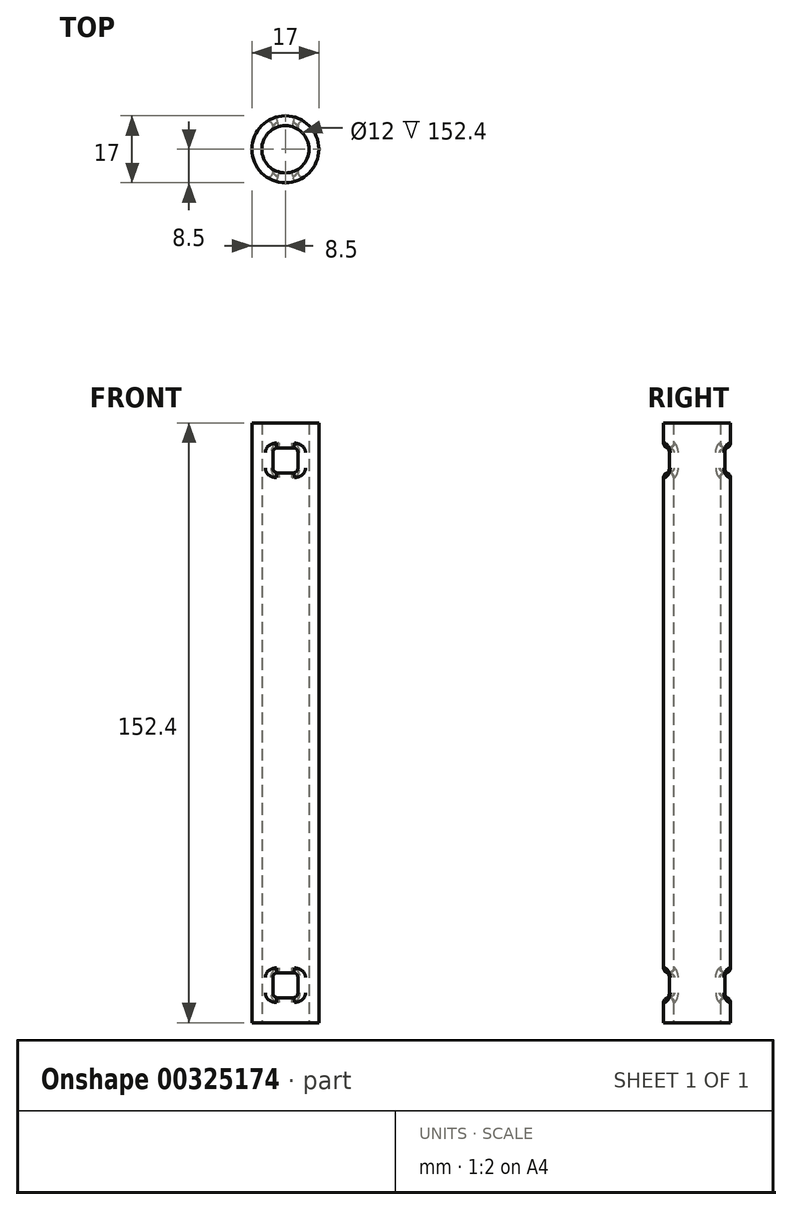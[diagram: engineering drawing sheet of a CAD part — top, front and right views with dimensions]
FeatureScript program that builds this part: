
annotation { "Feature Type Name" : "Feature", "Feature Type Description" : "" }
export const myFeature = defineFeature(function(context is Context, id is Id, definition is map)
    precondition{}
    {
        {
            var Q0;
            Q0=qCreatedBy(makeId("Top.planeOp"),FACE);
            var sketch = newSketch(context, id + "F0", { "sketchPlane" : qUnion([Q0])});
            skCircle(sketch, "E0", {"center": v(0, 0) * mm, "radius": 8.5 * mm});
            skCircle(sketch, "E1", {"center": v(0, 0) * mm, "radius": 6 * mm});
            skSolve(sketch);
        }
        {
            var Q0;
            Q0=makeQuery(id+"F0.imprint","IMPRINT",FACE,{"disambiguationData":[TD([[makeQuery(id+"F0.imprint","IMPRINT",EDGE,{"derivedFrom":sQuery(id+"F0.wireOp",EDGE,"E0")}),1.0]])]});
            extrude(context, id + "F1", {"entities" : qUnion([Q0]), "depth" : 152.4 * mm});
        }
        {
            var Q0;
            Q0=qCreatedBy(makeId("Front.planeOp"),FACE);
            var sketch = newSketch(context, id + "F2", { "sketchPlane" : qUnion([Q0])});
            skLineSegment(sketch, "E2.bottom", {"start": v(3.17, 12.7) * mm, "end": v(-3.18, 12.7) * mm});
            skLineSegment(sketch, "E2.top", {"start": v(3.17, 6.35) * mm, "end": v(-3.18, 6.35) * mm});
            skLineSegment(sketch, "E2.left", {"start": v(3.17, 12.7) * mm, "end": v(3.17, 6.35) * mm});
            skLineSegment(sketch, "E2.right", {"start": v(-3.18, 12.7) * mm, "end": v(-3.18, 6.35) * mm});
            skPoint(sketch, "E2.middle", {"position": v(0, 9.53) * mm});
            skLineSegment(sketch, "E3.bottom", {"start": v(3.17, 146.05) * mm, "end": v(-3.18, 146.05) * mm});
            skLineSegment(sketch, "E3.top", {"start": v(3.17, 139.7) * mm, "end": v(-3.18, 139.7) * mm});
            skLineSegment(sketch, "E3.left", {"start": v(3.17, 146.05) * mm, "end": v(3.17, 139.7) * mm});
            skLineSegment(sketch, "E3.right", {"start": v(-3.18, 146.05) * mm, "end": v(-3.18, 139.7) * mm});
            skPoint(sketch, "E3.middle", {"position": v(0, 142.88) * mm});
            skSolve(sketch);
        }
        {
            var Q0;
            Q0=makeQuery(id+"F2.imprint","IMPRINT",FACE,{"disambiguationData":[TD([[makeQuery(id+"F2.imprint","IMPRINT",EDGE,{"derivedFrom":sQuery(id+"F2.wireOp",EDGE,"E3.bottom")}),1.0]])]});
            var Q1;
            Q1=makeQuery(id+"F2.imprint","IMPRINT",FACE,{"disambiguationData":[TD([[makeQuery(id+"F2.imprint","IMPRINT",EDGE,{"derivedFrom":sQuery(id+"F2.wireOp",EDGE,"E2.bottom")}),1.0]])]});
            extrude(context, id + "F3", {"entities" : qUnion([Q0, Q1]), "operationType" : NewBodyOperationType.REMOVE, "depth" : 25.4 * mm, "hasSecondDirection" : true, "secondDirectionOppositeDirection" : true, "secondDirectionDepth" : 25.4 * mm});
        }
        {
            var Q0;
            Q0=makeQuery(id+"F3.boolean.opBoolean","COPY",FACE,{"disambiguationData":[OD(1.0)],"derivedFrom":makeQuery(id+"F3.opExtrude","SWEPT_FACE",FACE,{"disambiguationData":[OSD([sQuery(id+"F2.wireOp",EDGE,"E3.bottom")])]})});
            var Q1;
            Q1=makeQuery(id+"F3.boolean.opBoolean","INTERSECT",EDGE,{"disambiguationData":[OD(1.0)],"derivedFrom":[makeQuery(id+"F1.opExtrude","SWEPT_FACE",FACE,{"disambiguationData":[OSD([sQuery(id+"F0.wireOp",EDGE,"E1")])]}),makeQuery(id+"F3.opExtrude","SWEPT_FACE",FACE,{"disambiguationData":[OSD([sQuery(id+"F2.wireOp",EDGE,"E3.top")])]})]});
            var Q2;
            Q2=makeQuery(id+"F3.boolean.opBoolean","COPY",FACE,{"disambiguationData":[OD(0.0)],"derivedFrom":makeQuery(id+"F3.opExtrude","SWEPT_FACE",FACE,{"disambiguationData":[OSD([sQuery(id+"F2.wireOp",EDGE,"E3.right")])]})});
            var Q3;
            Q3=makeQuery(id+"F3.boolean.opBoolean","INTERSECT",EDGE,{"disambiguationData":[OD(0.0)],"derivedFrom":[makeQuery(id+"F1.opExtrude","SWEPT_FACE",FACE,{"disambiguationData":[OSD([sQuery(id+"F0.wireOp",EDGE,"E1")])]}),makeQuery(id+"F3.opExtrude","SWEPT_FACE",FACE,{"disambiguationData":[OSD([sQuery(id+"F2.wireOp",EDGE,"E3.right")])]})]});
            var Q4;
            Q4=makeQuery(id+"F3.boolean.opBoolean","INTERSECT",EDGE,{"disambiguationData":[OD(1.0)],"derivedFrom":[makeQuery(id+"F1.opExtrude","SWEPT_FACE",FACE,{"disambiguationData":[OSD([sQuery(id+"F0.wireOp",EDGE,"E0")])]}),makeQuery(id+"F3.opExtrude","SWEPT_FACE",FACE,{"disambiguationData":[OSD([sQuery(id+"F2.wireOp",EDGE,"E3.top")])]})]});
            var Q5;
            Q5=makeQuery(id+"F3.boolean.opBoolean","INTERSECT",EDGE,{"disambiguationData":[OD(1.0)],"derivedFrom":[makeQuery(id+"F1.opExtrude","SWEPT_FACE",FACE,{"disambiguationData":[OSD([sQuery(id+"F0.wireOp",EDGE,"E1")])]}),makeQuery(id+"F3.opExtrude","SWEPT_FACE",FACE,{"disambiguationData":[OSD([sQuery(id+"F2.wireOp",EDGE,"E3.bottom")])]})]});
            var Q6;
            Q6=makeQuery(id+"F3.boolean.opBoolean","COPY",FACE,{"disambiguationData":[OD(0.0)],"derivedFrom":makeQuery(id+"F3.opExtrude","SWEPT_FACE",FACE,{"disambiguationData":[OSD([sQuery(id+"F2.wireOp",EDGE,"E3.left")])]})});
            var Q7;
            Q7=makeQuery(id+"F3.boolean.opBoolean","COPY",FACE,{"disambiguationData":[OD(1.0)],"derivedFrom":makeQuery(id+"F3.opExtrude","SWEPT_FACE",FACE,{"disambiguationData":[OSD([sQuery(id+"F2.wireOp",EDGE,"E3.right")])]})});
            var Q8;
            Q8=makeQuery(id+"F3.boolean.opBoolean","COPY",FACE,{"disambiguationData":[OD(1.0)],"derivedFrom":makeQuery(id+"F3.opExtrude","SWEPT_FACE",FACE,{"disambiguationData":[OSD([sQuery(id+"F2.wireOp",EDGE,"E3.left")])]})});
            var Q9;
            Q9=makeQuery(id+"F3.boolean.opBoolean","COPY",FACE,{"disambiguationData":[OD(1.0)],"derivedFrom":makeQuery(id+"F3.opExtrude","SWEPT_FACE",FACE,{"disambiguationData":[OSD([sQuery(id+"F2.wireOp",EDGE,"E3.top")])]})});
            var Q10;
            Q10=makeQuery(id+"F3.boolean.opBoolean","COPY",FACE,{"disambiguationData":[OD(0.0)],"derivedFrom":makeQuery(id+"F3.opExtrude","SWEPT_FACE",FACE,{"disambiguationData":[OSD([sQuery(id+"F2.wireOp",EDGE,"E3.bottom")])]})});
            var Q11;
            Q11=makeQuery(id+"F3.boolean.opBoolean","COPY",FACE,{"disambiguationData":[OD(0.0)],"derivedFrom":makeQuery(id+"F3.opExtrude","SWEPT_FACE",FACE,{"disambiguationData":[OSD([sQuery(id+"F2.wireOp",EDGE,"E3.top")])]})});
            var Q12;
            Q12=makeQuery(id+"F3.boolean.opBoolean","INTERSECT",EDGE,{"disambiguationData":[OD(1.0)],"derivedFrom":[makeQuery(id+"F1.opExtrude","SWEPT_FACE",FACE,{"disambiguationData":[OSD([sQuery(id+"F0.wireOp",EDGE,"E0")])]}),makeQuery(id+"F3.opExtrude","SWEPT_FACE",FACE,{"disambiguationData":[OSD([sQuery(id+"F2.wireOp",EDGE,"E3.right")])]})]});
            var Q13;
            Q13=makeQuery(id+"F3.boolean.opBoolean","INTERSECT",EDGE,{"disambiguationData":[OD(1.0)],"derivedFrom":[makeQuery(id+"F1.opExtrude","SWEPT_FACE",FACE,{"disambiguationData":[OSD([sQuery(id+"F0.wireOp",EDGE,"E0")])]}),makeQuery(id+"F3.opExtrude","SWEPT_FACE",FACE,{"disambiguationData":[OSD([sQuery(id+"F2.wireOp",EDGE,"E3.bottom")])]})]});
            var Q14;
            Q14=makeQuery(id+"F3.boolean.opBoolean","INTERSECT",EDGE,{"disambiguationData":[OD(0.0)],"derivedFrom":[makeQuery(id+"F1.opExtrude","SWEPT_FACE",FACE,{"disambiguationData":[OSD([sQuery(id+"F0.wireOp",EDGE,"E0")])]}),makeQuery(id+"F3.opExtrude","SWEPT_FACE",FACE,{"disambiguationData":[OSD([sQuery(id+"F2.wireOp",EDGE,"E3.right")])]})]});
            var Q15;
            Q15=makeQuery(id+"F3.boolean.opBoolean","INTERSECT",EDGE,{"disambiguationData":[OD(0.0)],"derivedFrom":[makeQuery(id+"F1.opExtrude","SWEPT_FACE",FACE,{"disambiguationData":[OSD([sQuery(id+"F0.wireOp",EDGE,"E0")])]}),makeQuery(id+"F3.opExtrude","SWEPT_FACE",FACE,{"disambiguationData":[OSD([sQuery(id+"F2.wireOp",EDGE,"E3.bottom")])]})]});
            var Q16;
            Q16=makeQuery(id+"F3.boolean.opBoolean","INTERSECT",EDGE,{"disambiguationData":[OD(0.0)],"derivedFrom":[makeQuery(id+"F1.opExtrude","SWEPT_FACE",FACE,{"disambiguationData":[OSD([sQuery(id+"F0.wireOp",EDGE,"E0")])]}),makeQuery(id+"F3.opExtrude","SWEPT_FACE",FACE,{"disambiguationData":[OSD([sQuery(id+"F2.wireOp",EDGE,"E3.left")])]})]});
            var Q17;
            Q17=makeQuery(id+"F3.boolean.opBoolean","INTERSECT",EDGE,{"disambiguationData":[OD(0.0)],"derivedFrom":[makeQuery(id+"F1.opExtrude","SWEPT_FACE",FACE,{"disambiguationData":[OSD([sQuery(id+"F0.wireOp",EDGE,"E1")])]}),makeQuery(id+"F3.opExtrude","SWEPT_FACE",FACE,{"disambiguationData":[OSD([sQuery(id+"F2.wireOp",EDGE,"E3.top")])]})]});
            var Q18;
            Q18=makeQuery(id+"F3.boolean.opBoolean","INTERSECT",EDGE,{"disambiguationData":[OD(0.0)],"derivedFrom":[makeQuery(id+"F1.opExtrude","SWEPT_FACE",FACE,{"disambiguationData":[OSD([sQuery(id+"F0.wireOp",EDGE,"E1")])]}),makeQuery(id+"F3.opExtrude","SWEPT_FACE",FACE,{"disambiguationData":[OSD([sQuery(id+"F2.wireOp",EDGE,"E3.bottom")])]})]});
            var Q19;
            Q19=makeQuery(id+"F3.boolean.opBoolean","INTERSECT",EDGE,{"disambiguationData":[OD(0.0)],"derivedFrom":[makeQuery(id+"F1.opExtrude","SWEPT_FACE",FACE,{"disambiguationData":[OSD([sQuery(id+"F0.wireOp",EDGE,"E0")])]}),makeQuery(id+"F3.opExtrude","SWEPT_FACE",FACE,{"disambiguationData":[OSD([sQuery(id+"F2.wireOp",EDGE,"E3.top")])]})]});
            var Q20;
            Q20=makeQuery(id+"F3.boolean.opBoolean","INTERSECT",EDGE,{"disambiguationData":[OD(1.0)],"derivedFrom":[makeQuery(id+"F1.opExtrude","SWEPT_FACE",FACE,{"disambiguationData":[OSD([sQuery(id+"F0.wireOp",EDGE,"E1")])]}),makeQuery(id+"F3.opExtrude","SWEPT_FACE",FACE,{"disambiguationData":[OSD([sQuery(id+"F2.wireOp",EDGE,"E3.right")])]})]});
            var Q21;
            Q21=makeQuery(id+"F3.boolean.opBoolean","COPY",EDGE,{"disambiguationData":[OD(0.0)],"derivedFrom":makeQuery(id+"F3.opExtrude","SWEPT_EDGE",EDGE,{"disambiguationData":[OSD([sQuery(id+"F2.wireOp",EDGE,"E3.bottom"),sQuery(id+"F2.wireOp",EDGE,"E3.right")])]})});
            var Q22;
            Q22=makeQuery(id+"F3.boolean.opBoolean","COPY",EDGE,{"disambiguationData":[OD(1.0)],"derivedFrom":makeQuery(id+"F3.opExtrude","SWEPT_EDGE",EDGE,{"disambiguationData":[OSD([sQuery(id+"F2.wireOp",EDGE,"E3.top"),sQuery(id+"F2.wireOp",EDGE,"E3.left")])]})});
            var Q23;
            Q23=makeQuery(id+"F3.boolean.opBoolean","COPY",EDGE,{"disambiguationData":[OD(1.0)],"derivedFrom":makeQuery(id+"F3.opExtrude","SWEPT_EDGE",EDGE,{"disambiguationData":[OSD([sQuery(id+"F2.wireOp",EDGE,"E3.bottom"),sQuery(id+"F2.wireOp",EDGE,"E3.right")])]})});
            var Q24;
            Q24=makeQuery(id+"F3.boolean.opBoolean","INTERSECT",EDGE,{"disambiguationData":[OD(1.0)],"derivedFrom":[makeQuery(id+"F1.opExtrude","SWEPT_FACE",FACE,{"disambiguationData":[OSD([sQuery(id+"F0.wireOp",EDGE,"E0")])]}),makeQuery(id+"F3.opExtrude","SWEPT_FACE",FACE,{"disambiguationData":[OSD([sQuery(id+"F2.wireOp",EDGE,"E3.left")])]})]});
            var Q25;
            Q25=makeQuery(id+"F3.boolean.opBoolean","COPY",EDGE,{"disambiguationData":[OD(0.0)],"derivedFrom":makeQuery(id+"F3.opExtrude","SWEPT_EDGE",EDGE,{"disambiguationData":[OSD([sQuery(id+"F2.wireOp",EDGE,"E3.bottom"),sQuery(id+"F2.wireOp",EDGE,"E3.left")])]})});
            var Q26;
            Q26=makeQuery(id+"F3.boolean.opBoolean","INTERSECT",EDGE,{"disambiguationData":[OD(1.0)],"derivedFrom":[makeQuery(id+"F1.opExtrude","SWEPT_FACE",FACE,{"disambiguationData":[OSD([sQuery(id+"F0.wireOp",EDGE,"E1")])]}),makeQuery(id+"F3.opExtrude","SWEPT_FACE",FACE,{"disambiguationData":[OSD([sQuery(id+"F2.wireOp",EDGE,"E3.left")])]})]});
            var Q27;
            Q27=makeQuery(id+"F3.boolean.opBoolean","COPY",EDGE,{"disambiguationData":[OD(0.0)],"derivedFrom":makeQuery(id+"F3.opExtrude","SWEPT_EDGE",EDGE,{"disambiguationData":[OSD([sQuery(id+"F2.wireOp",EDGE,"E3.top"),sQuery(id+"F2.wireOp",EDGE,"E3.left")])]})});
            var Q28;
            Q28=makeQuery(id+"F3.boolean.opBoolean","COPY",EDGE,{"disambiguationData":[OD(0.0)],"derivedFrom":makeQuery(id+"F3.opExtrude","SWEPT_EDGE",EDGE,{"disambiguationData":[OSD([sQuery(id+"F2.wireOp",EDGE,"E3.top"),sQuery(id+"F2.wireOp",EDGE,"E3.right")])]})});
            var Q29;
            Q29=makeQuery(id+"F3.boolean.opBoolean","INTERSECT",EDGE,{"disambiguationData":[OD(0.0)],"derivedFrom":[makeQuery(id+"F1.opExtrude","SWEPT_FACE",FACE,{"disambiguationData":[OSD([sQuery(id+"F0.wireOp",EDGE,"E1")])]}),makeQuery(id+"F3.opExtrude","SWEPT_FACE",FACE,{"disambiguationData":[OSD([sQuery(id+"F2.wireOp",EDGE,"E3.left")])]})]});
            var Q30;
            Q30=makeQuery(id+"F3.boolean.opBoolean","COPY",EDGE,{"disambiguationData":[OD(1.0)],"derivedFrom":makeQuery(id+"F3.opExtrude","SWEPT_EDGE",EDGE,{"disambiguationData":[OSD([sQuery(id+"F2.wireOp",EDGE,"E3.bottom"),sQuery(id+"F2.wireOp",EDGE,"E3.left")])]})});
            var Q31;
            Q31=makeQuery(id+"F3.boolean.opBoolean","COPY",EDGE,{"disambiguationData":[OD(1.0)],"derivedFrom":makeQuery(id+"F3.opExtrude","SWEPT_EDGE",EDGE,{"disambiguationData":[OSD([sQuery(id+"F2.wireOp",EDGE,"E3.top"),sQuery(id+"F2.wireOp",EDGE,"E3.right")])]})});
            var Q32;
            Q32=makeQuery(id+"F3.boolean.opBoolean","INTERSECT",EDGE,{"disambiguationData":[OD(0.0)],"derivedFrom":[makeQuery(id+"F1.opExtrude","SWEPT_FACE",FACE,{"disambiguationData":[OSD([sQuery(id+"F0.wireOp",EDGE,"E0")])]}),makeQuery(id+"F3.opExtrude","SWEPT_FACE",FACE,{"disambiguationData":[OSD([sQuery(id+"F2.wireOp",EDGE,"E2.bottom")])]})]});
            var Q33;
            Q33=makeQuery(id+"F3.boolean.opBoolean","INTERSECT",EDGE,{"disambiguationData":[OD(0.0)],"derivedFrom":[makeQuery(id+"F1.opExtrude","SWEPT_FACE",FACE,{"disambiguationData":[OSD([sQuery(id+"F0.wireOp",EDGE,"E1")])]}),makeQuery(id+"F3.opExtrude","SWEPT_FACE",FACE,{"disambiguationData":[OSD([sQuery(id+"F2.wireOp",EDGE,"E2.right")])]})]});
            var Q34;
            Q34=makeQuery(id+"F3.boolean.opBoolean","INTERSECT",EDGE,{"disambiguationData":[OD(0.0)],"derivedFrom":[makeQuery(id+"F1.opExtrude","SWEPT_FACE",FACE,{"disambiguationData":[OSD([sQuery(id+"F0.wireOp",EDGE,"E1")])]}),makeQuery(id+"F3.opExtrude","SWEPT_FACE",FACE,{"disambiguationData":[OSD([sQuery(id+"F2.wireOp",EDGE,"E2.bottom")])]})]});
            var Q35;
            Q35=makeQuery(id+"F3.boolean.opBoolean","INTERSECT",EDGE,{"disambiguationData":[OD(0.0)],"derivedFrom":[makeQuery(id+"F1.opExtrude","SWEPT_FACE",FACE,{"disambiguationData":[OSD([sQuery(id+"F0.wireOp",EDGE,"E0")])]}),makeQuery(id+"F3.opExtrude","SWEPT_FACE",FACE,{"disambiguationData":[OSD([sQuery(id+"F2.wireOp",EDGE,"E2.top")])]})]});
            var Q36;
            Q36=makeQuery(id+"F3.boolean.opBoolean","INTERSECT",EDGE,{"disambiguationData":[OD(1.0)],"derivedFrom":[makeQuery(id+"F1.opExtrude","SWEPT_FACE",FACE,{"disambiguationData":[OSD([sQuery(id+"F0.wireOp",EDGE,"E1")])]}),makeQuery(id+"F3.opExtrude","SWEPT_FACE",FACE,{"disambiguationData":[OSD([sQuery(id+"F2.wireOp",EDGE,"E2.bottom")])]})]});
            var Q37;
            Q37=makeQuery(id+"F3.boolean.opBoolean","INTERSECT",EDGE,{"disambiguationData":[OD(1.0)],"derivedFrom":[makeQuery(id+"F1.opExtrude","SWEPT_FACE",FACE,{"disambiguationData":[OSD([sQuery(id+"F0.wireOp",EDGE,"E1")])]}),makeQuery(id+"F3.opExtrude","SWEPT_FACE",FACE,{"disambiguationData":[OSD([sQuery(id+"F2.wireOp",EDGE,"E2.top")])]})]});
            var Q38;
            Q38=makeQuery(id+"F3.boolean.opBoolean","INTERSECT",EDGE,{"disambiguationData":[OD(1.0)],"derivedFrom":[makeQuery(id+"F1.opExtrude","SWEPT_FACE",FACE,{"disambiguationData":[OSD([sQuery(id+"F0.wireOp",EDGE,"E1")])]}),makeQuery(id+"F3.opExtrude","SWEPT_FACE",FACE,{"disambiguationData":[OSD([sQuery(id+"F2.wireOp",EDGE,"E2.right")])]})]});
            var Q39;
            Q39=makeQuery(id+"F3.boolean.opBoolean","INTERSECT",EDGE,{"disambiguationData":[OD(1.0)],"derivedFrom":[makeQuery(id+"F1.opExtrude","SWEPT_FACE",FACE,{"disambiguationData":[OSD([sQuery(id+"F0.wireOp",EDGE,"E0")])]}),makeQuery(id+"F3.opExtrude","SWEPT_FACE",FACE,{"disambiguationData":[OSD([sQuery(id+"F2.wireOp",EDGE,"E2.bottom")])]})]});
            var Q40;
            Q40=makeQuery(id+"F3.boolean.opBoolean","INTERSECT",EDGE,{"disambiguationData":[OD(0.0)],"derivedFrom":[makeQuery(id+"F1.opExtrude","SWEPT_FACE",FACE,{"disambiguationData":[OSD([sQuery(id+"F0.wireOp",EDGE,"E0")])]}),makeQuery(id+"F3.opExtrude","SWEPT_FACE",FACE,{"disambiguationData":[OSD([sQuery(id+"F2.wireOp",EDGE,"E2.right")])]})]});
            var Q41;
            Q41=makeQuery(id+"F3.boolean.opBoolean","COPY",EDGE,{"disambiguationData":[OD(1.0)],"derivedFrom":makeQuery(id+"F3.opExtrude","SWEPT_EDGE",EDGE,{"disambiguationData":[OSD([sQuery(id+"F2.wireOp",EDGE,"E2.bottom"),sQuery(id+"F2.wireOp",EDGE,"E2.left")])]})});
            var Q42;
            Q42=makeQuery(id+"F3.boolean.opBoolean","COPY",EDGE,{"disambiguationData":[OD(0.0)],"derivedFrom":makeQuery(id+"F3.opExtrude","SWEPT_EDGE",EDGE,{"disambiguationData":[OSD([sQuery(id+"F2.wireOp",EDGE,"E2.bottom"),sQuery(id+"F2.wireOp",EDGE,"E2.right")])]})});
            var Q43;
            Q43=makeQuery(id+"F3.boolean.opBoolean","COPY",EDGE,{"disambiguationData":[OD(0.0)],"derivedFrom":makeQuery(id+"F3.opExtrude","SWEPT_EDGE",EDGE,{"disambiguationData":[OSD([sQuery(id+"F2.wireOp",EDGE,"E2.top"),sQuery(id+"F2.wireOp",EDGE,"E2.right")])]})});
            var Q44;
            Q44=makeQuery(id+"F3.boolean.opBoolean","COPY",EDGE,{"disambiguationData":[OD(1.0)],"derivedFrom":makeQuery(id+"F3.opExtrude","SWEPT_EDGE",EDGE,{"disambiguationData":[OSD([sQuery(id+"F2.wireOp",EDGE,"E2.bottom"),sQuery(id+"F2.wireOp",EDGE,"E2.right")])]})});
            var Q45;
            Q45=makeQuery(id+"F3.boolean.opBoolean","COPY",EDGE,{"disambiguationData":[OD(1.0)],"derivedFrom":makeQuery(id+"F3.opExtrude","SWEPT_EDGE",EDGE,{"disambiguationData":[OSD([sQuery(id+"F2.wireOp",EDGE,"E2.top"),sQuery(id+"F2.wireOp",EDGE,"E2.left")])]})});
            var Q46;
            Q46=makeQuery(id+"F3.boolean.opBoolean","INTERSECT",EDGE,{"disambiguationData":[OD(0.0)],"derivedFrom":[makeQuery(id+"F1.opExtrude","SWEPT_FACE",FACE,{"disambiguationData":[OSD([sQuery(id+"F0.wireOp",EDGE,"E1")])]}),makeQuery(id+"F3.opExtrude","SWEPT_FACE",FACE,{"disambiguationData":[OSD([sQuery(id+"F2.wireOp",EDGE,"E2.top")])]})]});
            var Q47;
            Q47=makeQuery(id+"F3.boolean.opBoolean","INTERSECT",EDGE,{"disambiguationData":[OD(0.0)],"derivedFrom":[makeQuery(id+"F1.opExtrude","SWEPT_FACE",FACE,{"disambiguationData":[OSD([sQuery(id+"F0.wireOp",EDGE,"E1")])]}),makeQuery(id+"F3.opExtrude","SWEPT_FACE",FACE,{"disambiguationData":[OSD([sQuery(id+"F2.wireOp",EDGE,"E2.left")])]})]});
            var Q48;
            Q48=makeQuery(id+"F3.boolean.opBoolean","INTERSECT",EDGE,{"disambiguationData":[OD(1.0)],"derivedFrom":[makeQuery(id+"F1.opExtrude","SWEPT_FACE",FACE,{"disambiguationData":[OSD([sQuery(id+"F0.wireOp",EDGE,"E0")])]}),makeQuery(id+"F3.opExtrude","SWEPT_FACE",FACE,{"disambiguationData":[OSD([sQuery(id+"F2.wireOp",EDGE,"E2.right")])]})]});
            var Q49;
            Q49=makeQuery(id+"F3.boolean.opBoolean","INTERSECT",EDGE,{"disambiguationData":[OD(0.0)],"derivedFrom":[makeQuery(id+"F1.opExtrude","SWEPT_FACE",FACE,{"disambiguationData":[OSD([sQuery(id+"F0.wireOp",EDGE,"E0")])]}),makeQuery(id+"F3.opExtrude","SWEPT_FACE",FACE,{"disambiguationData":[OSD([sQuery(id+"F2.wireOp",EDGE,"E2.left")])]})]});
            var Q50;
            Q50=makeQuery(id+"F3.boolean.opBoolean","COPY",EDGE,{"disambiguationData":[OD(0.0)],"derivedFrom":makeQuery(id+"F3.opExtrude","SWEPT_EDGE",EDGE,{"disambiguationData":[OSD([sQuery(id+"F2.wireOp",EDGE,"E2.bottom"),sQuery(id+"F2.wireOp",EDGE,"E2.left")])]})});
            var Q51;
            Q51=makeQuery(id+"F3.boolean.opBoolean","INTERSECT",EDGE,{"disambiguationData":[OD(1.0)],"derivedFrom":[makeQuery(id+"F1.opExtrude","SWEPT_FACE",FACE,{"disambiguationData":[OSD([sQuery(id+"F0.wireOp",EDGE,"E1")])]}),makeQuery(id+"F3.opExtrude","SWEPT_FACE",FACE,{"disambiguationData":[OSD([sQuery(id+"F2.wireOp",EDGE,"E2.left")])]})]});
            var Q52;
            Q52=makeQuery(id+"F3.boolean.opBoolean","COPY",EDGE,{"disambiguationData":[OD(1.0)],"derivedFrom":makeQuery(id+"F3.opExtrude","SWEPT_EDGE",EDGE,{"disambiguationData":[OSD([sQuery(id+"F2.wireOp",EDGE,"E2.top"),sQuery(id+"F2.wireOp",EDGE,"E2.right")])]})});
            var Q53;
            Q53=makeQuery(id+"F3.boolean.opBoolean","INTERSECT",EDGE,{"disambiguationData":[OD(1.0)],"derivedFrom":[makeQuery(id+"F1.opExtrude","SWEPT_FACE",FACE,{"disambiguationData":[OSD([sQuery(id+"F0.wireOp",EDGE,"E0")])]}),makeQuery(id+"F3.opExtrude","SWEPT_FACE",FACE,{"disambiguationData":[OSD([sQuery(id+"F2.wireOp",EDGE,"E2.top")])]})]});
            var Q54;
            Q54=makeQuery(id+"F3.boolean.opBoolean","INTERSECT",EDGE,{"disambiguationData":[OD(1.0)],"derivedFrom":[makeQuery(id+"F1.opExtrude","SWEPT_FACE",FACE,{"disambiguationData":[OSD([sQuery(id+"F0.wireOp",EDGE,"E0")])]}),makeQuery(id+"F3.opExtrude","SWEPT_FACE",FACE,{"disambiguationData":[OSD([sQuery(id+"F2.wireOp",EDGE,"E2.left")])]})]});
            var Q55;
            Q55=makeQuery(id+"F3.boolean.opBoolean","COPY",EDGE,{"disambiguationData":[OD(0.0)],"derivedFrom":makeQuery(id+"F3.opExtrude","SWEPT_EDGE",EDGE,{"disambiguationData":[OSD([sQuery(id+"F2.wireOp",EDGE,"E2.top"),sQuery(id+"F2.wireOp",EDGE,"E2.left")])]})});
            fillet(context, id + "F4", {"entities" : qUnion([Q0, Q1, Q2, Q3, Q4, Q5, Q6, Q7, Q8, Q9, Q10, Q11, Q12, Q13, Q14, Q15, Q16, Q17, Q18, Q19, Q20, Q21, Q22, Q23, Q24, Q25, Q26, Q27, Q28, Q29, Q30, Q31, Q32, Q33, Q34, Q35, Q36, Q37, Q38, Q39, Q40, Q41, Q42, Q43, Q44, Q45, Q46, Q47, Q48, Q49, Q50, Q51, Q52, Q53, Q54, Q55]), "radius" : 1.2 * mm, "tangentPropagation" : true, "allowEdgeOverflow" : false});
        }
    });
